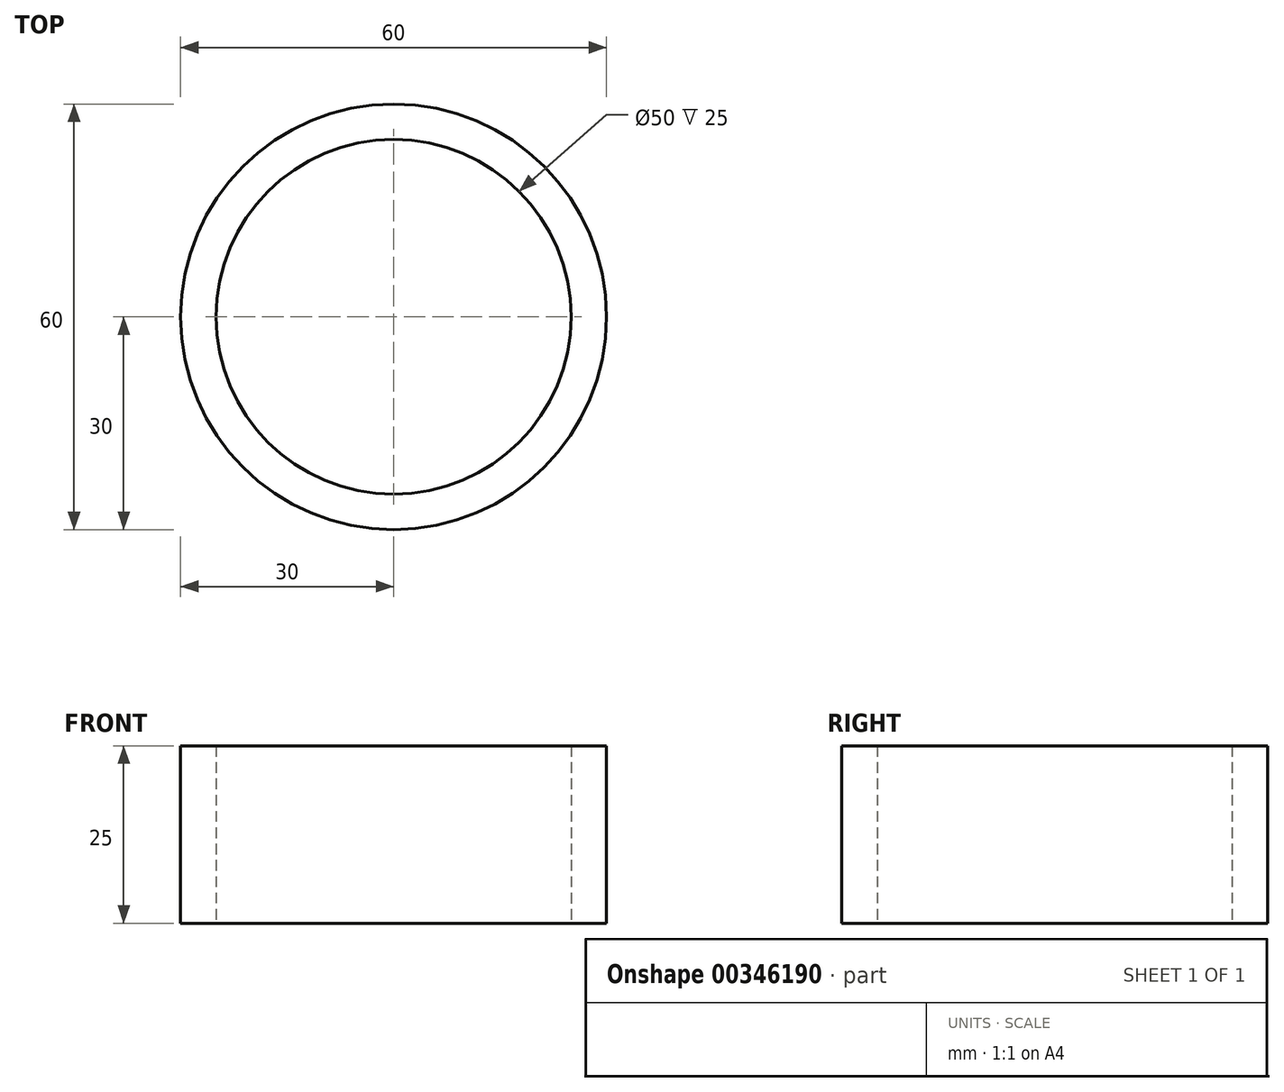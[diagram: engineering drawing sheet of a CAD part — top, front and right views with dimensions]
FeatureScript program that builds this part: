
annotation { "Feature Type Name" : "Feature", "Feature Type Description" : "" }
export const myFeature = defineFeature(function(context is Context, id is Id, definition is map)
    precondition{}
    {
        {
            var Q0;
            Q0=qCreatedBy(makeId("Top.planeOp"),FACE);
            var sketch = newSketch(context, id + "F0", { "sketchPlane" : qUnion([Q0])});
            skCircle(sketch, "E0", {"center": v(0, 0) * mm, "radius": 25 * mm});
            skCircle(sketch, "E1", {"center": v(0, 0) * mm, "radius": 30 * mm});
            skSolve(sketch);
        }
        {
            var Q0;
            Q0=makeQuery(id+"F0.imprint","IMPRINT",FACE,{"disambiguationData":[TD([[makeQuery(id+"F0.imprint","IMPRINT",EDGE,{"derivedFrom":sQuery(id+"F0.wireOp",EDGE,"E0")}),-1.0]])]});
            extrude(context, id + "F1", {"entities" : qUnion([Q0]), "depth" : 25 * mm});
        }
    });
